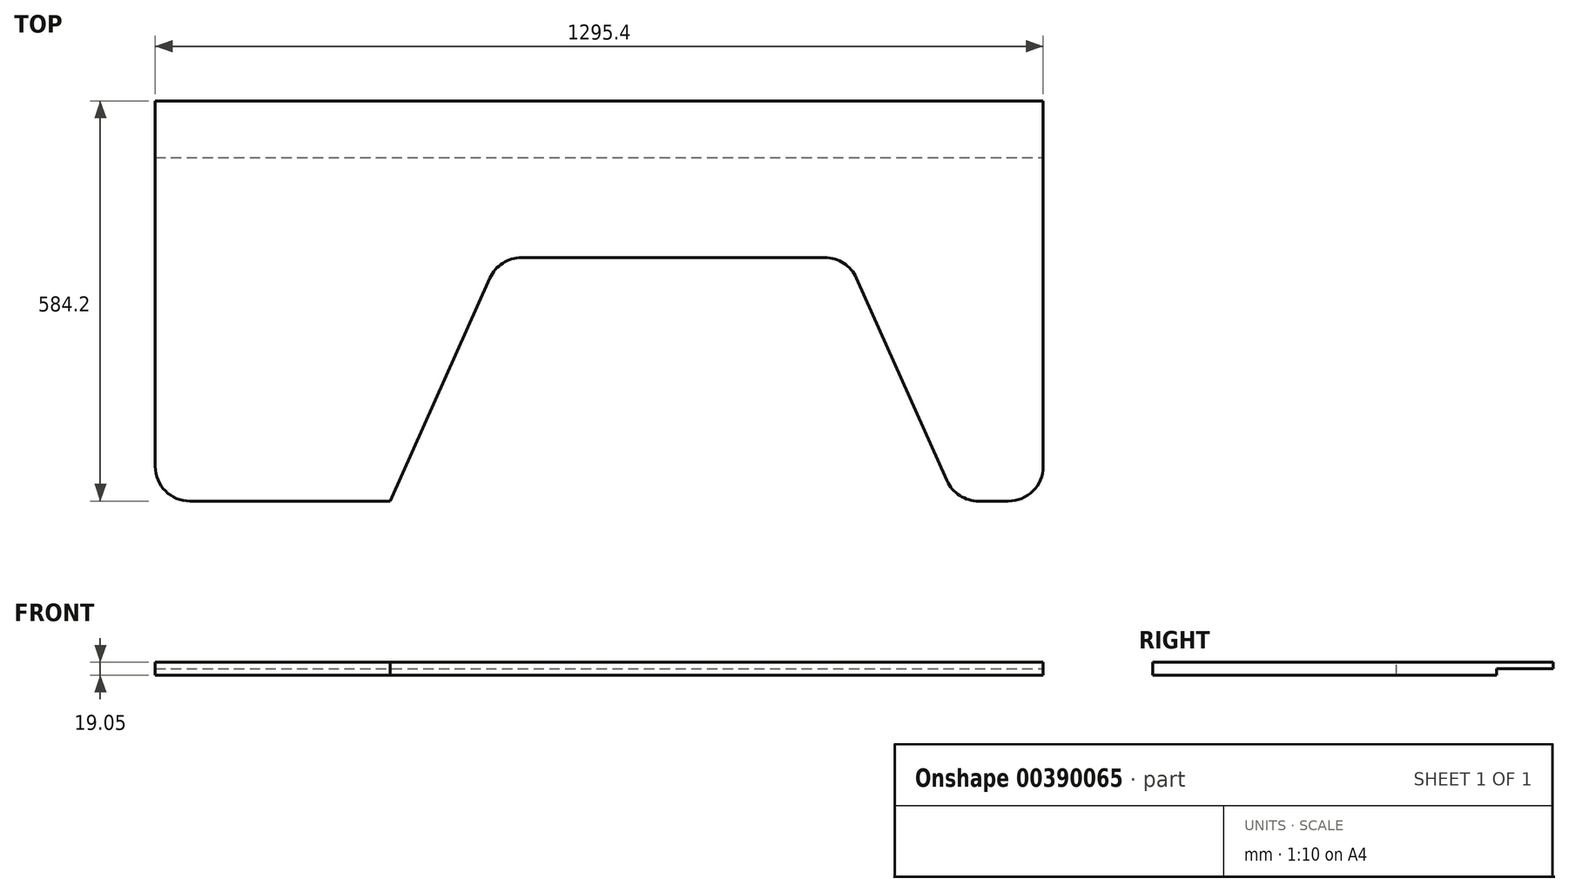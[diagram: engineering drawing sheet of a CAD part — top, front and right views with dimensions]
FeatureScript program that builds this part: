
annotation { "Feature Type Name" : "Feature", "Feature Type Description" : "" }
export const myFeature = defineFeature(function(context is Context, id is Id, definition is map)
    precondition{}
    {
        {
            var Q0;
            Q0=qCreatedBy(makeId("Top.planeOp"),FACE);
            var sketch = newSketch(context, id + "F0", { "sketchPlane" : qUnion([Q0])});
            skLineSegment(sketch, "E0.bottom", {"start": v(-647.7, 292.1) * mm, "end": v(647.7, 292.1) * mm});
            skLineSegment(sketch, "E0.top", {"start": v(-647.7, -292.1) * mm, "end": v(647.7, -292.1) * mm});
            skLineSegment(sketch, "E0.left", {"start": v(-647.7, 292.1) * mm, "end": v(-647.7, -292.1) * mm});
            skLineSegment(sketch, "E0.right", {"start": v(647.7, 292.1) * mm, "end": v(647.7, -292.1) * mm});
            skLineSegment(sketch, "E1", {"start": v(647.7, 292.1) * mm, "end": v(-647.7, -292.1) * mm, "construction": true});
            skLineSegment(sketch, "E2", {"start": v(0, 292.1) * mm, "end": v(0, -292.1) * mm, "construction": true});
            skSolve(sketch);
        }
        {
            var Q0;
            Q0 = qSketchRegion(id + "F0", true);
            extrude(context, id + "F1", {"entities" : qUnion([Q0]), "depth" : 19.05 * mm, "offsetDistance" : 25.4 * mm});
        }
        {
            var Q0;
            Q0=makeQuery(id+"F1.opExtrude","CAP_FACE",FACE,{"disambiguationData":[OSD([sQuery(id+"F0.wireOp",EDGE,"E0.bottom"),sQuery(id+"F0.wireOp",EDGE,"E0.top"),sQuery(id+"F0.wireOp",EDGE,"E0.left"),sQuery(id+"F0.wireOp",EDGE,"E0.right")])],"isStart":false});
            var sketch = newSketch(context, id + "F2", { "sketchPlane" : qUnion([Q0])});
            skLineSegment(sketch, "E3", {"start": v(-304.8, -292.1) * mm, "end": v(-159.48, 33.4) * mm});
            skLineSegment(sketch, "E4", {"start": v(-113.1, 63.5) * mm, "end": v(329, 63.5) * mm});
            skLineSegment(sketch, "E5", {"start": v(375.38, 33.4) * mm, "end": v(520.7, -292.1) * mm});
            skLineSegment(sketch, "E6", {"start": v(520.7, -292.1) * mm, "end": v(-304.8, -292.1) * mm});
            skPoint(sketch, "E7.visualSharp", {"position": v(-146.05, 63.5) * mm});
            skArc(sketch, "E7.filletArc", {"start": v(-113.1, 63.5) * mm, "mid": v(-140.74, 55.32) * mm, "end": v(-159.48, 33.4) * mm});
            skPoint(sketch, "E8.visualSharp", {"position": v(361.95, 63.5) * mm});
            skArc(sketch, "E8.filletArc", {"start": v(375.38, 33.4) * mm, "mid": v(356.64, 55.32) * mm, "end": v(329, 63.5) * mm});
            skSolve(sketch);
        }
        {
            var Q0;
            Q0 = qSketchRegion(id + "F2", true);
            extrude(context, id + "F3", {"entities" : qUnion([Q0]), "operationType" : NewBodyOperationType.REMOVE, "oppositeDirection" : true, "depth" : 25.4 * mm, "offsetDistance" : 25.4 * mm});
        }
        {
            var Q0;
            Q0=makeQuery(id+"F3.boolean.opBoolean","COPY",EDGE,{"derivedFrom":makeQuery(id+"F3.opExtrude","SWEPT_EDGE",EDGE,{"disambiguationData":[OSD([sQuery(id+"F0.wireOp",EDGE,"E0.top"),sQuery(id+"F2.wireOp",EDGE,"E3"),sQuery(id+"F2.wireOp",EDGE,"E6")])]})});
            var Q1;
            Q1=makeQuery(id+"F3.boolean.opBoolean","COPY",EDGE,{"derivedFrom":makeQuery(id+"F3.opExtrude","SWEPT_EDGE",EDGE,{"disambiguationData":[OSD([sQuery(id+"F0.wireOp",EDGE,"E0.top"),sQuery(id+"F2.wireOp",EDGE,"E5"),sQuery(id+"F2.wireOp",EDGE,"E6")])]})});
            var Q2;
            Q2=makeQuery(id+"F1.opExtrude","SWEPT_EDGE",EDGE,{"disambiguationData":[OSD([sQuery(id+"F0.wireOp",EDGE,"E0.top"),sQuery(id+"F0.wireOp",EDGE,"E0.right")])]});
            var Q3;
            Q3=makeQuery(id+"F1.opExtrude","SWEPT_EDGE",EDGE,{"disambiguationData":[OSD([sQuery(id+"F0.wireOp",EDGE,"E0.top"),sQuery(id+"F0.wireOp",EDGE,"E0.left")])]});
            fillet(context, id + "F4", {"entities" : qUnion([Q0, Q1, Q2, Q3]), "radius" : 50.8 * mm, "tangentPropagation" : true, "allowEdgeOverflow" : false});
        }
        {
            var Q0;
            Q0=makeQuery(id+"F1.opExtrude","SWEPT_FACE",FACE,{"disambiguationData":[OSD([sQuery(id+"F0.wireOp",EDGE,"E0.right")])]});
            var sketch = newSketch(context, id + "F5", { "sketchPlane" : qUnion([Q0])});
            skLineSegment(sketch, "E9.bottom", {"start": v(292.1, 0) * mm, "end": v(209.55, 0) * mm});
            skLineSegment(sketch, "E9.top", {"start": v(292.1, 9.53) * mm, "end": v(209.55, 9.53) * mm});
            skLineSegment(sketch, "E9.left", {"start": v(292.1, 0) * mm, "end": v(292.1, 9.53) * mm});
            skLineSegment(sketch, "E9.right", {"start": v(209.55, 0) * mm, "end": v(209.55, 9.53) * mm});
            skSolve(sketch);
        }
        {
            var Q0;
            Q0=makeQuery(id+"F5.imprint","IMPRINT",FACE,{"disambiguationData":[TD([[makeQuery(id+"F5.imprint","IMPRINT",EDGE,{"derivedFrom":sQuery(id+"F5.wireOp",EDGE,"E9.bottom")}),-1.0]])]});
            extrude(context, id + "F6", {"entities" : qUnion([Q0]), "operationType" : NewBodyOperationType.REMOVE, "endBound" : BoundingType.THROUGH_ALL, "oppositeDirection" : true, "depth" : 25.4 * mm, "offsetDistance" : 25.4 * mm});
        }
    });
